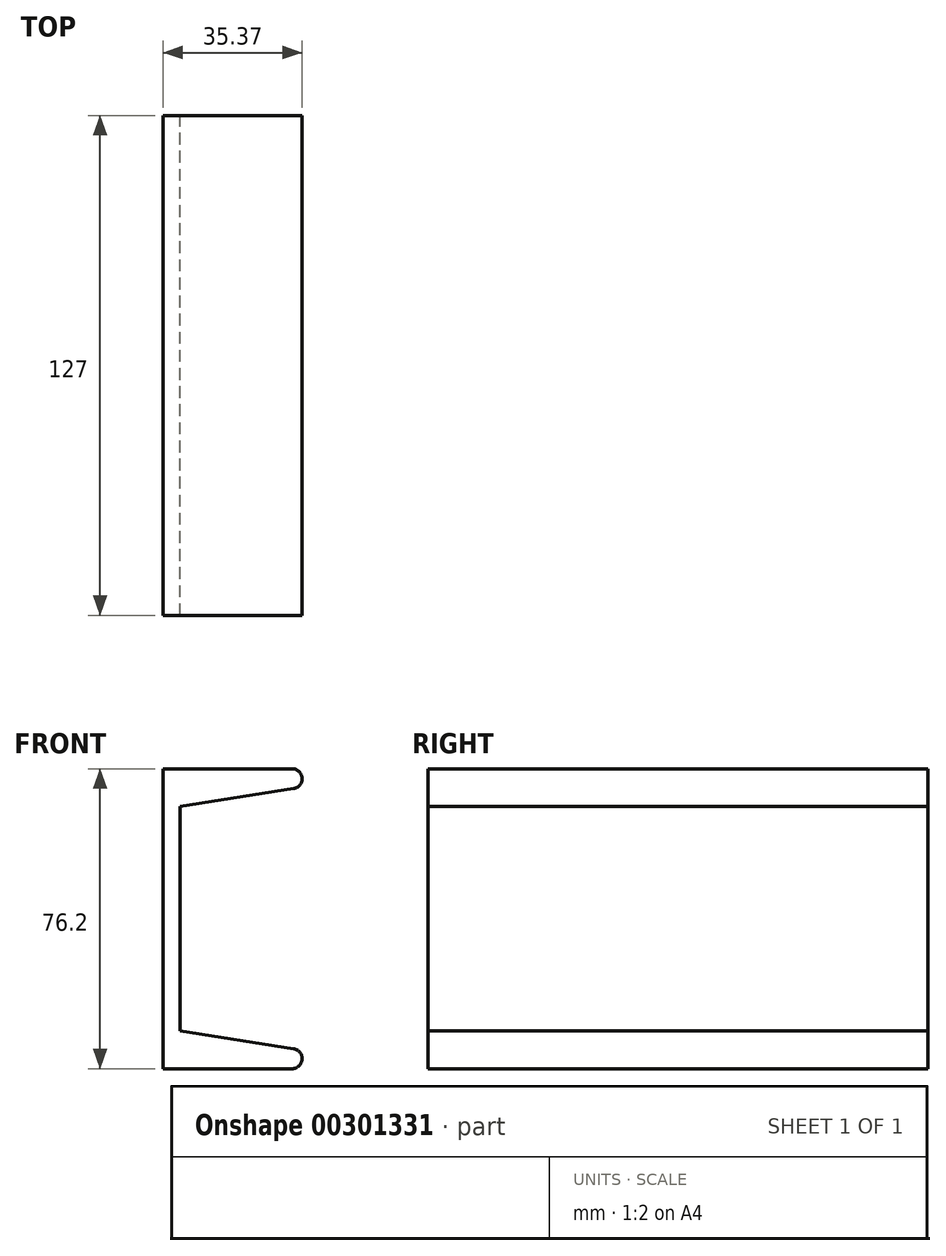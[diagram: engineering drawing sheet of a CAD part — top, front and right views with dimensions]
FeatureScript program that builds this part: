
annotation { "Feature Type Name" : "Feature", "Feature Type Description" : "" }
export const myFeature = defineFeature(function(context is Context, id is Id, definition is map)
    precondition{}
    {
        {
            var Q0;
            Q0=qCreatedBy(makeId("Front.planeOp"),FACE);
            var sketch = newSketch(context, id + "F0", { "sketchPlane" : qUnion([Q0])});
            skLineSegment(sketch, "E0", {"start": v(0, 38.1) * mm, "end": v(0, 76.2) * mm});
            skLineSegment(sketch, "E1", {"start": v(0, 76.2) * mm, "end": v(32.83, 76.2) * mm});
            skLineSegment(sketch, "E2", {"start": v(4.32, 66.57) * mm, "end": v(4.32, 38.1) * mm});
            skLineSegment(sketch, "E3", {"start": v(33.22, 71.15) * mm, "end": v(4.32, 66.57) * mm});
            skPoint(sketch, "E4.endSnap0", {"position": v(0, 38.1) * mm});
            skPoint(sketch, "E5.orphan", {"position": v(0, 0) * mm});
            skArc(sketch, "E6", {"start": v(33.22, 71.15) * mm, "mid": v(35.36, 73.86) * mm, "end": v(32.83, 76.2) * mm});
            skLineSegment(sketch, "E7.MirrorCS", {"start": v(0, 38.1) * mm, "end": v(0, 0) * mm});
            skLineSegment(sketch, "E8.MirrorCS", {"start": v(4.32, 9.63) * mm, "end": v(4.32, 38.1) * mm});
            skLineSegment(sketch, "E9.MirrorCS", {"start": v(33.22, 5.05) * mm, "end": v(4.32, 9.63) * mm});
            skLineSegment(sketch, "E10.MirrorCS", {"start": v(0, 0) * mm, "end": v(32.83, 0) * mm});
            skArc(sketch, "E11.MirrorCS", {"start": v(33.22, 5.05) * mm, "mid": v(35.36, 2.34) * mm, "end": v(32.83, 0) * mm});
            skSolve(sketch);
        }
        {
            var Q0;
            Q0=makeQuery(id+"F0.imprint","IMPRINT",FACE,{"disambiguationData":[TD([[makeQuery(id+"F0.imprint","IMPRINT",EDGE,{"derivedFrom":sQuery(id+"F0.wireOp",EDGE,"E0")}),-1.0]])]});
            extrude(context, id + "F1", {"entities" : qUnion([Q0]), "depth" : 127 * mm});
        }
    });
